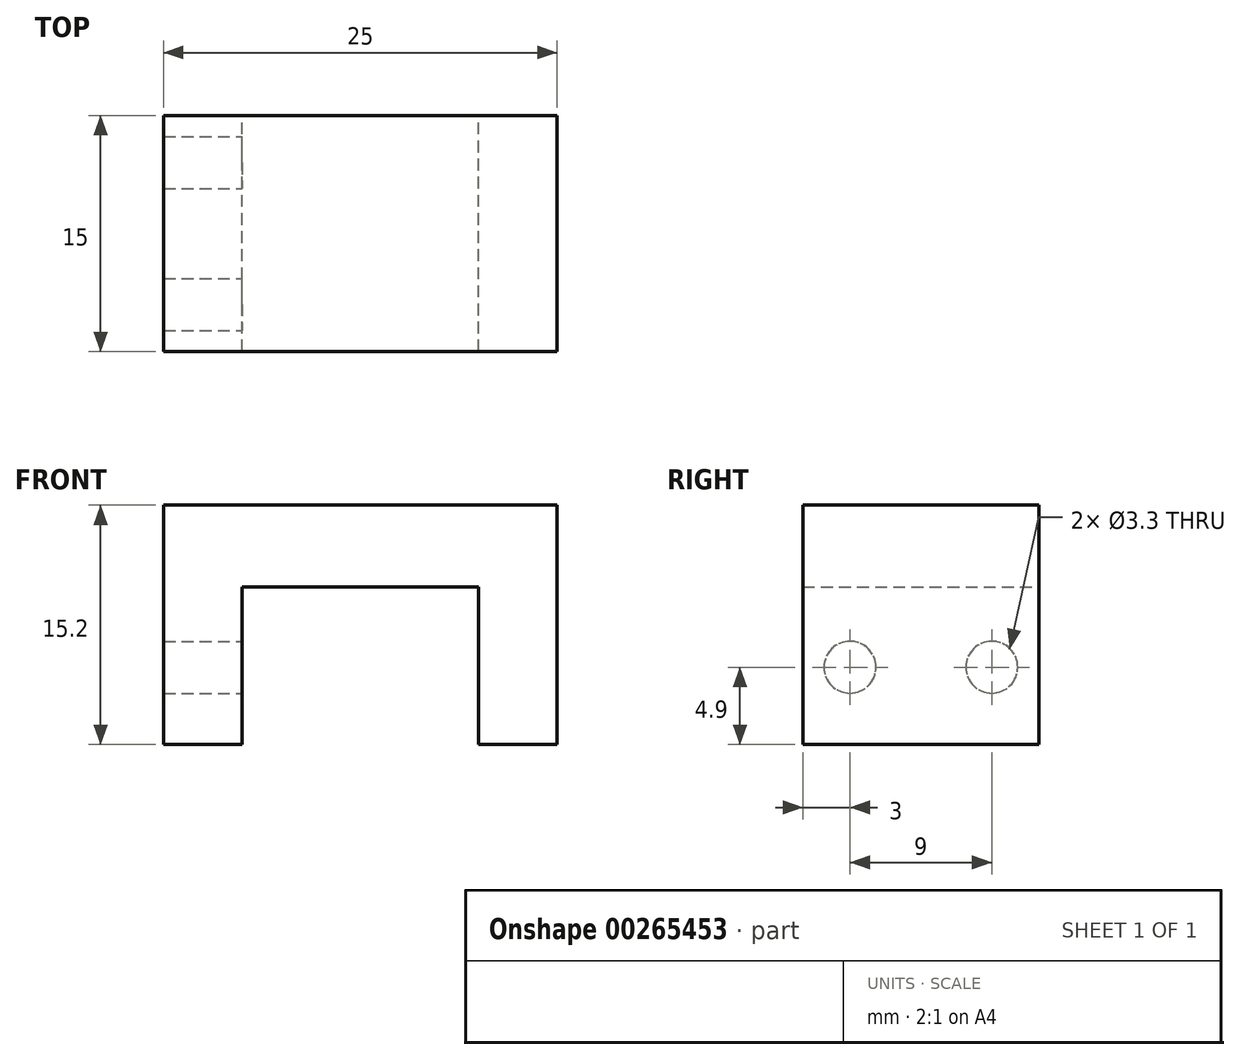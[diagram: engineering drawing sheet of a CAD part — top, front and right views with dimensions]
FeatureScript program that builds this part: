
annotation { "Feature Type Name" : "Feature", "Feature Type Description" : "" }
export const myFeature = defineFeature(function(context is Context, id is Id, definition is map)
    precondition{}
    {
        {
            var Q0;
            Q0=qCreatedBy(makeId("Front.planeOp"),FACE);
            var sketch = newSketch(context, id + "F0", { "sketchPlane" : qUnion([Q0])});
            skLineSegment(sketch, "E0.bottom", {"start": v(-12.5, 0) * mm, "end": v(12.5, 0) * mm});
            skLineSegment(sketch, "E0.left", {"start": v(-12.5, 0) * mm, "end": v(-12.5, -15.2) * mm});
            skLineSegment(sketch, "E0.right", {"start": v(12.5, 0) * mm, "end": v(12.5, -15.2) * mm});
            skLineSegment(sketch, "E1.top", {"start": v(-7.5, -5.2) * mm, "end": v(7.5, -5.2) * mm});
            skLineSegment(sketch, "E1.left", {"start": v(-7.5, -15.2) * mm, "end": v(-7.5, -5.2) * mm});
            skLineSegment(sketch, "E1.right", {"start": v(7.5, -15.2) * mm, "end": v(7.5, -5.2) * mm});
            skLineSegment(sketch, "E2", {"start": v(-12.5, -15.2) * mm, "end": v(-7.5, -15.2) * mm});
            skLineSegment(sketch, "E3", {"start": v(7.5, -15.2) * mm, "end": v(12.5, -15.2) * mm});
            skSolve(sketch);
        }
        {
            var Q0;
            Q0=makeQuery(id+"F0.imprint","IMPRINT",FACE,{"disambiguationData":[TD([[makeQuery(id+"F0.imprint","IMPRINT",EDGE,{"derivedFrom":sQuery(id+"F0.wireOp",EDGE,"E0.bottom")}),-1.0]])]});
            extrude(context, id + "F1", {"entities" : qUnion([Q0]), "endBound" : BoundingType.SYMMETRIC, "depth" : 15 * mm});
        }
        {
            var Q0;
            Q0=qCreatedBy(makeId("Right.planeOp"),FACE);
            var sketch = newSketch(context, id + "F2", { "sketchPlane" : qUnion([Q0])});
            skLineSegment(sketch, "E4", {"start": v(7.5, -10.3) * mm, "end": v(-7.5, -10.3) * mm, "construction": true});
            skPoint(sketch, "E5", {"position": v(4.5, -10.3) * mm});
            skPoint(sketch, "E6", {"position": v(-4.5, -10.3) * mm});
            skSolve(sketch);
        }
        {
            var Q0;
            Q0=sQuery(id+"F2.wireOp",VERTEX,"E5");
            var Q1;
            Q1=sQuery(id+"F2.wireOp",VERTEX,"E6");
            var Q2;
            Q2=makeQuery(id+"F1.opExtrude","SWEPT_BODY",BODY,{"disambiguationData":[OSD([sQuery(id+"F0.wireOp",EDGE,"E0.bottom"),sQuery(id+"F0.wireOp",EDGE,"E0.left"),sQuery(id+"F0.wireOp",EDGE,"E0.right"),sQuery(id+"F0.wireOp",EDGE,"E1.top"),sQuery(id+"F0.wireOp",EDGE,"E1.left"),sQuery(id+"F0.wireOp",EDGE,"E1.right"),sQuery(id+"F0.wireOp",EDGE,"E2"),sQuery(id+"F0.wireOp",EDGE,"E3")])]});
            hole(context, id + "F3", {"style" : HoleStyle.SIMPLE, "endStyle" : HoleEndStyle.BLIND, "standardTappedOrClearance" : lookupTablePath({ "standard" : "ISO", "engagement" : "75%", "pitch" : "0.7 mm", "size" : "M4", "type" : "Tapped" }), "standardBlindInLast" : lookupTablePath({ "standard" : "ISO", "engagement" : "75%", "pitch" : "0.7 mm", "size" : "M4", "type" : "Tapped" }), "holeDiameter" : 3.3 * mm, "showTappedDepth" : true, "holeDepth" : 14.1 * mm, "tappedDepth" : 12 * mm, "tapClearance" : 3, "startFromSketch" : true, "locations" : qUnion([Q0, Q1]), "scope" : qUnion([Q2]), "majorDiameter" : 4 * mm});
        }
    });
